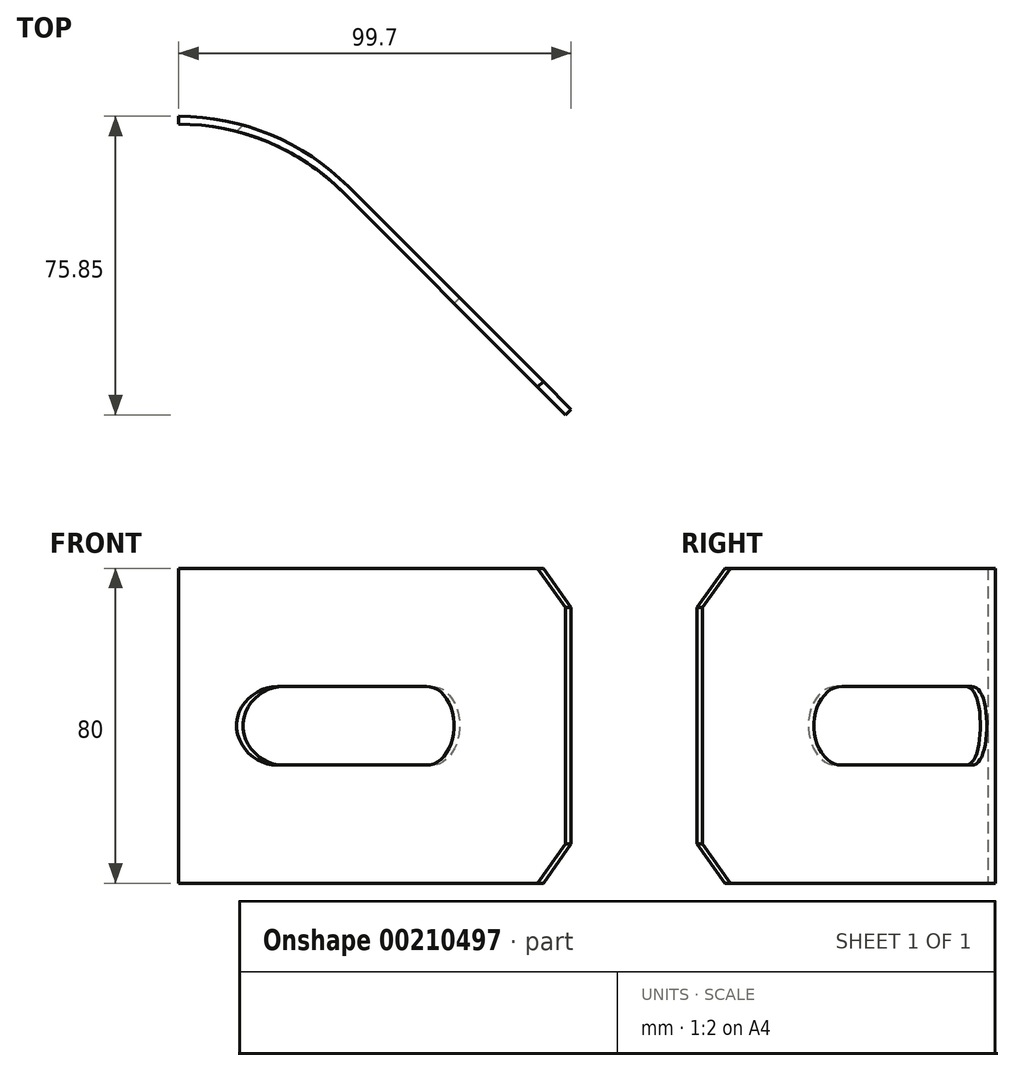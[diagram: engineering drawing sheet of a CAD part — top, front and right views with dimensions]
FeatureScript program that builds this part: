
annotation { "Feature Type Name" : "Feature", "Feature Type Description" : "" }
export const myFeature = defineFeature(function(context is Context, id is Id, definition is map)
    precondition{}
    {
        {
            var Q0;
            Q0=qCreatedBy(makeId("Right.planeOp"),FACE);
            var sketch = newSketch(context, id + "F0", { "sketchPlane" : qUnion([Q0])});
            skLineSegment(sketch, "E0.rect.bottom", {"start": v(61, 40) * mm, "end": v(59, 40) * mm});
            skLineSegment(sketch, "E0.rect.top", {"start": v(61, -40) * mm, "end": v(59, -40) * mm});
            skLineSegment(sketch, "E0.rect.left", {"start": v(61, 40) * mm, "end": v(61, -40) * mm});
            skLineSegment(sketch, "E0.rect.right", {"start": v(59, 40) * mm, "end": v(59, -40) * mm});
            skPoint(sketch, "E0.rect.middle", {"position": v(60, 0) * mm});
            skLineSegment(sketch, "E1", {"start": v(0, 40) * mm, "end": v(0, -40) * mm, "construction": true});
            skSolve(sketch);
        }
        {
            var Q0;
            Q0=makeQuery(id+"F0.imprint","IMPRINT",FACE,{"disambiguationData":[TD([[makeQuery(id+"F0.imprint","IMPRINT",EDGE,{"derivedFrom":sQuery(id+"F0.wireOp",EDGE,"E0.rect.bottom")}),1.0]])]});
            var Q1;
            Q1=sQuery(id+"F0.wireOp",EDGE,"E1");
            revolve(context, id + "F1", {"entities" : qUnion([Q0]), "axis" : qUnion([Q1]), "revolveType" : RevolveType.ONE_DIRECTION, "angle" : 45 * degree});
        }
        {
            var Q0;
            Q0=makeQuery(id+"F1.opRevolve","CAP_FACE",FACE,{"disambiguationData":[OSD([sQuery(id+"F0.wireOp",EDGE,"E0.rect.bottom"),sQuery(id+"F0.wireOp",EDGE,"E0.rect.top"),sQuery(id+"F0.wireOp",EDGE,"E0.rect.left"),sQuery(id+"F0.wireOp",EDGE,"E0.rect.right")])],"isStart":false});
            extrude(context, id + "F2", {"entities" : qUnion([Q0]), "operationType" : NewBodyOperationType.ADD, "depth" : 80 * mm});
        }
        {
            var Q0;
            Q0=makeQuery(id+"F2.opExtrude","SWEPT_FACE",FACE,{"disambiguationData":[OSD([sQuery(id+"F0.wireOp",EDGE,"E0.rect.left")])]});
            var sketch = newSketch(context, id + "F3", { "sketchPlane" : qUnion([Q0])});
            skLineSegment(sketch, "E2", {"start": v(20, 0) * mm, "end": v(-30, 0) * mm});
            skArc(sketch, "E3.0.startCap", {"start": v(20, 10) * mm, "mid": v(30, 0) * mm, "end": v(20, -10) * mm});
            skArc(sketch, "E3.0.endCap", {"start": v(-30, -10) * mm, "mid": v(-40, 0) * mm, "end": v(-30, 10) * mm});
            skLineSegment(sketch, "E3.0.left", {"start": v(20, -10) * mm, "end": v(-30, -10) * mm});
            skLineSegment(sketch, "E3.0.right", {"start": v(20, 10) * mm, "end": v(-30, 10) * mm});
            skSolve(sketch);
        }
        {
            var Q0;
            Q0=qSketchRegion(id+"F3",true);
            extrude(context, id + "F4", {"entities" : qUnion([Q0]), "operationType" : NewBodyOperationType.REMOVE, "endBound" : BoundingType.THROUGH_ALL, "oppositeDirection" : true, "depth" : 25 * mm});
        }
        {
            var Q0;
            Q0=makeQuery(id+"F2.opExtrude","CAP_EDGE",EDGE,{"disambiguationData":[OSD([sQuery(id+"F0.wireOp",EDGE,"E0.rect.bottom")])],"isStart":false});
            var Q1;
            Q1=makeQuery(id+"F2.opExtrude","CAP_EDGE",EDGE,{"disambiguationData":[OSD([sQuery(id+"F0.wireOp",EDGE,"E0.rect.top")])],"isStart":false});
            chamfer(context, id + "F5", {"entities" : qUnion([Q0, Q1]), "width" : 10 * mm, "tangentPropagation" : true});
        }
    });
